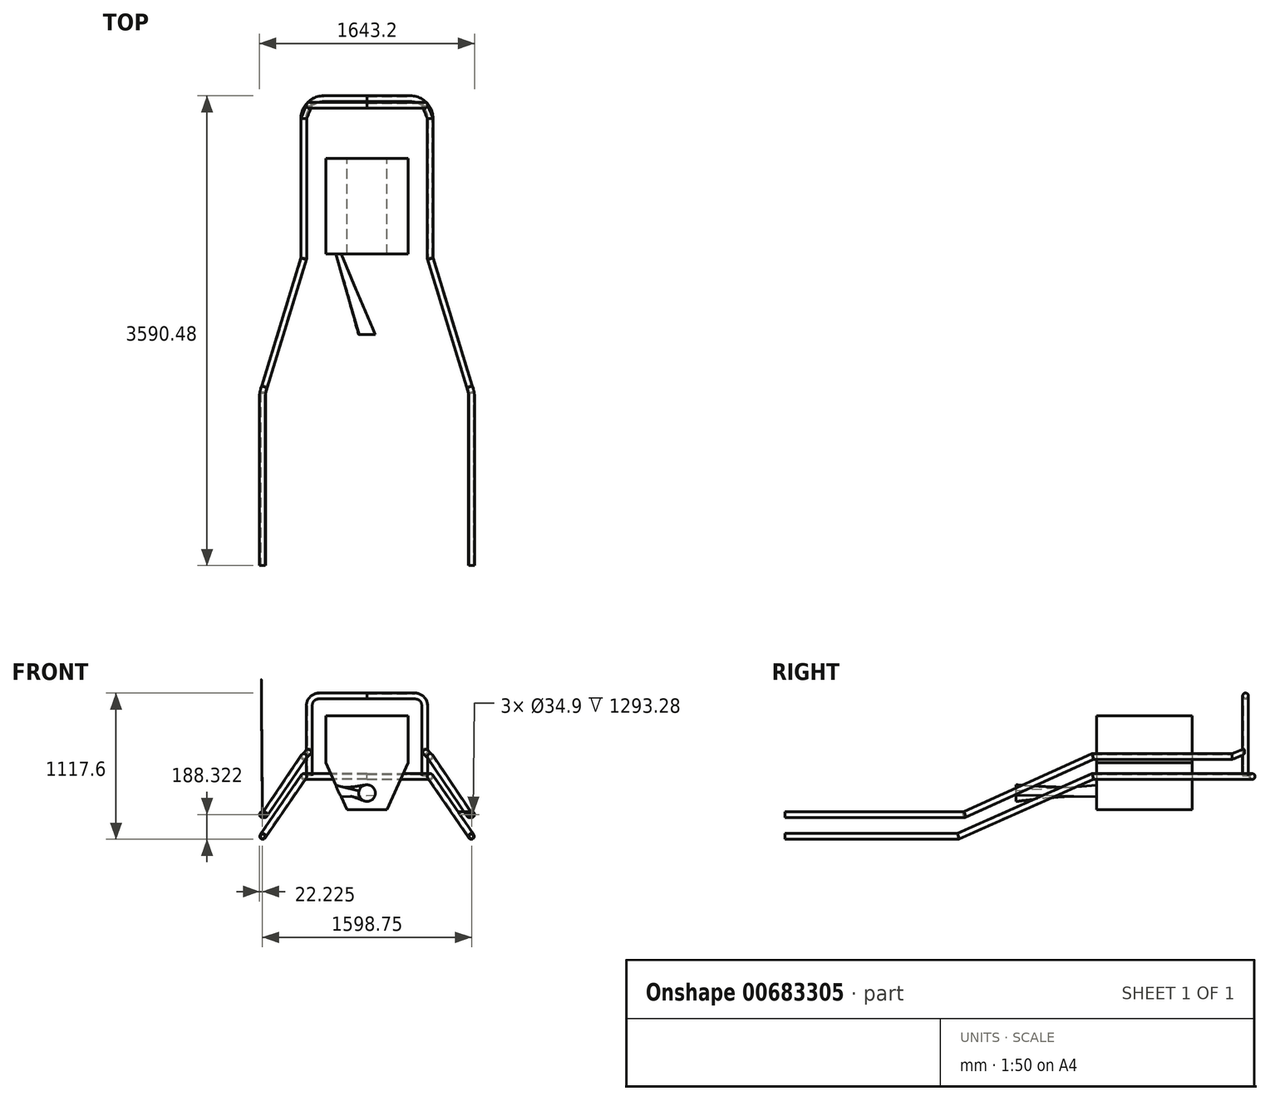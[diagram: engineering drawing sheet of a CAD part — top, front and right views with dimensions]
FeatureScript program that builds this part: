
annotation { "Feature Type Name" : "Feature", "Feature Type Description" : "" }
export const myFeature = defineFeature(function(context is Context, id is Id, definition is map)
    precondition{}
    {
        {
            var Q0;
            Q0=qCreatedBy(makeId("Front.planeOp"),FACE);
            var sketch = newSketch(context, id + "F0", { "sketchPlane" : qUnion([Q0])});
            skLineSegment(sketch, "E0", {"start": v(0, 0) * mm, "end": v(0, 717.55) * mm});
            skLineSegment(sketch, "E1", {"start": v(0, 717.55) * mm, "end": v(-314.33, 717.55) * mm});
            skLineSegment(sketch, "E2", {"start": v(-314.33, 717.55) * mm, "end": v(-314.33, 358.77) * mm});
            skLineSegment(sketch, "E3", {"start": v(0, 0) * mm, "end": v(-152.4, 0) * mm});
            skLineSegment(sketch, "E4", {"start": v(-314.33, 358.77) * mm, "end": v(-152.4, 0) * mm});
            skLineSegment(sketch, "E5.MirrorCS", {"start": v(0, 0) * mm, "end": v(152.4, 0) * mm});
            skLineSegment(sketch, "E6.MirrorCS", {"start": v(0, 717.55) * mm, "end": v(314.33, 717.55) * mm});
            skLineSegment(sketch, "E7.MirrorCS", {"start": v(314.33, 358.77) * mm, "end": v(152.4, 0) * mm});
            skLineSegment(sketch, "E8.MirrorCS", {"start": v(314.33, 717.55) * mm, "end": v(314.33, 358.77) * mm});
            skSolve(sketch);
        }
        {
            var Q0;
            Q0=makeQuery(id+"F0.imprint","IMPRINT",FACE,{"disambiguationData":[TD([[makeQuery(id+"F0.imprint","IMPRINT",EDGE,{"derivedFrom":sQuery(id+"F0.wireOp",EDGE,"E0")}),1.0]])]});
            var Q1;
            Q1=makeQuery(id+"F0.imprint","IMPRINT",FACE,{"disambiguationData":[TD([[makeQuery(id+"F0.imprint","IMPRINT",EDGE,{"derivedFrom":sQuery(id+"F0.wireOp",EDGE,"E0")}),-1.0]])]});
            extrude(context, id + "F1", {"entities" : qUnion([Q0, Q1]), "depth" : 730.25 * mm, "offsetDistance" : 25.4 * mm});
        }
        {
            var Q0;
            Q0=makeQuery(id+"F1.opExtrude","CAP_FACE",FACE,{"disambiguationData":[OSD([sQuery(id+"F0.wireOp",EDGE,"E1"),sQuery(id+"F0.wireOp",EDGE,"E2"),sQuery(id+"F0.wireOp",EDGE,"E3"),sQuery(id+"F0.wireOp",EDGE,"E4"),sQuery(id+"F0.wireOp",EDGE,"E5.MirrorCS"),sQuery(id+"F0.wireOp",EDGE,"E6.MirrorCS"),sQuery(id+"F0.wireOp",EDGE,"E7.MirrorCS"),sQuery(id+"F0.wireOp",EDGE,"E8.MirrorCS")])],"isStart":false});
            var sketch = newSketch(context, id + "F2", { "sketchPlane" : qUnion([Q0])});
            skCircle(sketch, "E9", {"center": v(0, 241.3) * mm, "radius": 242.89 * mm});
            skSolve(sketch);
        }
        {
            var Q0;
            Q0=makeQuery(id+"F2.imprint","IMPRINT",FACE,{"disambiguationData":[TD([[makeQuery(id+"F2.imprint","IMPRINT",EDGE,{"derivedFrom":makeQuery(id+"F1.opExtrude","CAP_EDGE",EDGE,{"disambiguationData":[OSD([sQuery(id+"F0.wireOp",EDGE,"E2")])],"isStart":false})}),1.0]])]});
            cPlane(context, id + "F3", {"entities" : qUnion([Q0]), "cplaneType" : CPlaneType.OFFSET, "offset" : 615.95 * mm, "width" : 152.4 * mm, "height" : 152.4 * mm});
        }
        {
            var Q0;
            Q0=qCreatedBy(id+"F3.planeOp",FACE);
            var sketch = newSketch(context, id + "F4", { "sketchPlane" : qUnion([Q0])});
            skCircle(sketch, "E10", {"center": v(0, 127) * mm, "radius": 63.5 * mm});
            skSolve(sketch);
        }
        {
            var Q1;
            {var subQ0=sQuery(id+"F2.wireOp",EDGE,"E9");var subQ1=makeQuery(id+"F1.opExtrude","CAP_EDGE",EDGE,{"disambiguationData":[OSD([sQuery(id+"F0.wireOp",EDGE,"E4")])],"isStart":false});var subQ2=makeQuery(id+"F2.imprint","INTERSECT",VERTEX,{"disambiguationData":[OD(1.0)],"derivedFrom":[subQ1,subQ0]});Q1=makeQuery(id+"F2.imprint","IMPRINT",FACE,{"disambiguationData":[TD([[makeQuery(id+"F2.imprint","IMPRINT",EDGE,{"disambiguationData":[TD([[subQ2,1.0]])],"derivedFrom":subQ0}),1.0]])]});}
            var Q2;
            Q2=makeQuery(id+"F4.imprint","IMPRINT",FACE,{"disambiguationData":[TD([[makeQuery(id+"F4.imprint","IMPRINT",EDGE,{"derivedFrom":sQuery(id+"F4.wireOp",EDGE,"E10")}),1.0]])]});
            loft(context, id + "F5", {"operationType" : NewBodyOperationType.ADD, "sheetProfilesArray" : [{ "sheetProfileEntities" : qUnion([Q1]) }, { "sheetProfileEntities" : qUnion([Q2]) }]});
        }
        {
            var Q0;
            Q0=makeQuery(id+"F1.opExtrude","SWEPT_FACE",FACE,{"disambiguationData":[OSD([sQuery(id+"F0.wireOp",EDGE,"E2")])]});
            cPlane(context, id + "F6", {"entities" : qUnion([Q0]), "cplaneType" : CPlaneType.OFFSET, "offset" : 317.5 * mm, "oppositeDirection" : true, "width" : 152.4 * mm, "height" : 152.4 * mm});
        }
        {
            var Q0;
            Q0=qCreatedBy(id+"F6.planeOp",FACE);
            var sketch = newSketch(context, id + "F7", { "sketchPlane" : qUnion([Q0])});
            skLineSegment(sketch, "E11.bottom", {"start": v(836.32, 471.65) * mm, "end": v(1187.86, 471.65) * mm});
            skLineSegment(sketch, "E11.top", {"start": v(836.32, 316.37) * mm, "end": v(1187.86, 316.37) * mm});
            skLineSegment(sketch, "E11.left", {"start": v(836.32, 471.65) * mm, "end": v(836.32, 316.37) * mm});
            skLineSegment(sketch, "E11.right", {"start": v(1187.86, 471.65) * mm, "end": v(1187.86, 316.37) * mm});
            skSolve(sketch);
        }
        {
            var Q0;
            Q0=makeQuery(id+"F7.imprint","IMPRINT",FACE,{"disambiguationData":[TD([[makeQuery(id+"F7.imprint","IMPRINT",EDGE,{"derivedFrom":sQuery(id+"F7.wireOp",EDGE,"E11.bottom")}),-1.0]])]});
            extrude(context, id + "F8", {"entities" : qUnion([Q0]), "operationType" : NewBodyOperationType.REMOVE, "endBound" : BoundingType.THROUGH_ALL, "oppositeDirection" : true, "depth" : 508 * mm, "offsetDistance" : 25.4 * mm, "hasSecondDirection" : true, "secondDirectionBound" : SecondDirectionBoundingType.THROUGH_ALL, "secondDirectionOppositeDirection" : false, "secondDirectionDepth" : 25.4 * mm});
        }
        {
            var Q0;
            Q0=makeQuery(id+"F1.opExtrude","SWEPT_FACE",FACE,{"disambiguationData":[OSD([sQuery(id+"F0.wireOp",EDGE,"E3"),sQuery(id+"F0.wireOp",EDGE,"E5.MirrorCS")])]});
            cPlane(context, id + "F9", {"entities" : qUnion([Q0]), "cplaneType" : CPlaneType.OFFSET, "offset" : 0 * mm, "width" : 152.4 * mm, "height" : 152.4 * mm});
        }
        {
            var Q0;
            Q0=qCreatedBy(id+"F9.planeOp",FACE);
            var sketch = newSketch(context, id + "F10", { "sketchPlane" : qUnion([Q0])});
            skLineSegment(sketch, "E12", {"start": v(0, 0) * mm, "end": v(0, -228.6) * mm});
            skLineSegment(sketch, "E13", {"start": v(0, -228.6) * mm, "end": v(-390.53, -228.6) * mm});
            skLineSegment(sketch, "E14", {"start": v(-517.52, -101.6) * mm, "end": v(-517.52, 730.25) * mm});
            skLineSegment(sketch, "E15", {"start": v(-669.92, 882.65) * mm, "end": v(-736.6, 882.65) * mm});
            skLineSegment(sketch, "E16", {"start": v(-889, 1035.05) * mm, "end": v(-889, 2711.45) * mm});
            skPoint(sketch, "E17.visualSharp", {"position": v(-517.52, -228.6) * mm});
            skArc(sketch, "E17.filletArc", {"start": v(-517.52, -101.6) * mm, "mid": v(-480.33, -191.4) * mm, "end": v(-390.53, -228.6) * mm});
            skPoint(sketch, "E18.visualSharp", {"position": v(-517.52, 882.65) * mm});
            skArc(sketch, "E18.filletArc", {"start": v(-517.52, 730.25) * mm, "mid": v(-562.16, 838.01) * mm, "end": v(-669.92, 882.65) * mm});
            skPoint(sketch, "E19.visualSharp", {"position": v(-889, 882.65) * mm});
            skArc(sketch, "E19.filletArc", {"start": v(-889, 1035.05) * mm, "mid": v(-844.36, 927.29) * mm, "end": v(-736.6, 882.65) * mm});
            skLineSegment(sketch, "E20.MirrorCS", {"start": v(669.92, 882.65) * mm, "end": v(736.6, 882.65) * mm});
            skArc(sketch, "E21.MirrorCS", {"start": v(517.52, -101.6) * mm, "mid": v(480.33, -191.4) * mm, "end": v(390.53, -228.6) * mm});
            skArc(sketch, "E22.MirrorCS", {"start": v(517.52, 730.25) * mm, "mid": v(562.16, 838.01) * mm, "end": v(669.92, 882.65) * mm});
            skArc(sketch, "E23.MirrorCS", {"start": v(889, 1035.05) * mm, "mid": v(844.36, 927.29) * mm, "end": v(736.6, 882.65) * mm});
            skLineSegment(sketch, "E24.MirrorCS", {"start": v(517.52, -101.6) * mm, "end": v(517.52, 730.25) * mm});
            skLineSegment(sketch, "E25.MirrorCS", {"start": v(0, -228.6) * mm, "end": v(390.53, -228.6) * mm});
            skLineSegment(sketch, "E26.MirrorCS", {"start": v(889, 1035.05) * mm, "end": v(889, 2711.45) * mm});
            skPoint(sketch, "E27.MirrorP", {"position": v(517.52, -228.6) * mm});
            skPoint(sketch, "E28.MirrorP", {"position": v(517.52, 882.65) * mm});
            skPoint(sketch, "E29.MirrorP", {"position": v(889, 882.65) * mm});
            skSolve(sketch);
        }
        {
            var Q0;
            Q0=qCreatedBy(id+"F3.planeOp",FACE);
            cPlane(context, id + "F11", {"entities" : qUnion([Q0]), "cplaneType" : CPlaneType.OFFSET, "offset" : 1365.25 * mm, "width" : 152.4 * mm, "height" : 152.4 * mm});
        }
        {
            var Q0;
            Q0=makeQuery(id+"F1.opExtrude","SWEPT_FACE",FACE,{"disambiguationData":[OSD([sQuery(id+"F0.wireOp",EDGE,"E2")])]});
            cPlane(context, id + "F12", {"entities" : qUnion([Q0]), "cplaneType" : CPlaneType.OFFSET, "offset" : 168.27 * mm, "width" : 152.4 * mm, "height" : 152.4 * mm});
        }
        {
            var Q0;
            Q0=qCreatedBy(id+"F12.planeOp",FACE);
            var sketch = newSketch(context, id + "F13", { "sketchPlane" : qUnion([Q0])});
            skLineSegment(sketch, "E30", {"start": v(-127, 0) * mm, "end": v(-127, 641.35) * mm});
            skLineSegment(sketch, "E31", {"start": v(25.4, 793.75) * mm, "end": v(728.15, 793.75) * mm});
            skPoint(sketch, "E32.visualSharp", {"position": v(-127, 793.75) * mm});
            skArc(sketch, "E32.filletArc", {"start": v(25.4, 793.75) * mm, "mid": v(-82.36, 749.11) * mm, "end": v(-127, 641.35) * mm});
            skSolve(sketch);
        }
        {
            var Q0;
            Q0=qCreatedBy(id+"F9.planeOp",FACE);
            cPlane(context, id + "F14", {"entities" : qUnion([Q0]), "cplaneType" : CPlaneType.OFFSET, "offset" : 254 * mm, "oppositeDirection" : true, "width" : 152.4 * mm, "height" : 152.4 * mm});
        }
        {
            var Q0;
            Q0=qCreatedBy(id+"F14.planeOp",FACE);
            var sketch = newSketch(context, id + "F15", { "sketchPlane" : qUnion([Q0])});
            skLineSegment(sketch, "E33", {"start": v(-482.6, 762) * mm, "end": v(-482.6, -304.8) * mm});
            skPoint(sketch, "E34.visualSharp", {"position": v(482.6, -457.2) * mm});
            skPoint(sketch, "E35.visualSharp", {"position": v(-482.6, -457.2) * mm});
            skArc(sketch, "E35.filletArc", {"start": v(-482.6, -304.8) * mm, "mid": v(-437.96, -412.56) * mm, "end": v(-330.2, -457.2) * mm});
            skLineSegment(sketch, "E36", {"start": v(-330.2, -457.2) * mm, "end": v(0, -457.2) * mm});
            skSolve(sketch);
        }
        {
            var Q0;
            Q0=makeQuery(id+"F1.opExtrude","CAP_EDGE",EDGE,{"disambiguationData":[OSD([sQuery(id+"F0.wireOp",EDGE,"E2")])],"isStart":false});
            cPlane(context, id + "F16", {"entities" : qUnion([Q0]), "cplaneType" : CPlaneType.LINE_ANGLE, "offset" : 25.4 * mm, "angle" : 17 * degree, "width" : 152.4 * mm, "height" : 152.4 * mm});
        }
        {
            var Q0;
            Q0=qCreatedBy(id+"F16.planeOp",FACE);
            cPlane(context, id + "F17", {"entities" : qUnion([Q0]), "cplaneType" : CPlaneType.OFFSET, "offset" : 151.64 * mm, "width" : 152.4 * mm, "height" : 152.4 * mm});
        }
        {
            var Q0;
            Q0=qCreatedBy(id+"F17.planeOp",FACE);
            var sketch = newSketch(context, id + "F18", { "sketchPlane" : qUnion([Q0])});
            skLineSegment(sketch, "E37", {"start": v(869.8, 254) * mm, "end": v(1945.04, -203.2) * mm});
            skSolve(sketch);
        }
        {
            var Q0;
            Q0=qCreatedBy(id+"F14.planeOp",FACE);
            cPlane(context, id + "F19", {"entities" : qUnion([Q0]), "cplaneType" : CPlaneType.OFFSET, "offset" : 457.2 * mm, "width" : 152.4 * mm, "height" : 152.4 * mm});
        }
        {
            var Q0;
            Q0=qCreatedBy(id+"F19.planeOp",FACE);
            var sketch = newSketch(context, id + "F20", { "sketchPlane" : qUnion([Q0])});
            skLineSegment(sketch, "E38", {"start": v(-796.97, 1790.25) * mm, "end": v(-796.97, 3111.05) * mm});
            skSolve(sketch);
        }
        {
            var Q0;
            Q0=qCreatedBy(makeId("Right.planeOp"),FACE);
            var sketch = newSketch(context, id + "F21", { "sketchPlane" : qUnion([Q0])});
            skCircle(sketch, "E39", {"center": v(457.2, 254) * mm, "radius": 22.23 * mm});
            skCircle(sketch, "E40", {"center": v(457.2, 254) * mm, "radius": 17.45 * mm});
            skSolve(sketch);
        }
        {
            var Q0;
            Q0=qCreatedBy(id+"F14.planeOp",FACE);
            cPlane(context, id + "F22", {"entities" : qUnion([Q0]), "cplaneType" : CPlaneType.OFFSET, "offset" : 152.4 * mm, "oppositeDirection" : true, "width" : 152.4 * mm, "height" : 152.4 * mm});
        }
        {
            var Q0;
            Q0=qCreatedBy(id+"F22.planeOp",FACE);
            var sketch = newSketch(context, id + "F23", { "sketchPlane" : qUnion([Q0])});
            skLineSegment(sketch, "E41", {"start": v(-482.6, -304.8) * mm, "end": v(-482.6, 762) * mm});
            skSolve(sketch);
        }
        {
            var Q0;
            Q0=qCreatedBy(id+"F17.planeOp",FACE);
            var sketch = newSketch(context, id + "F24", { "sketchPlane" : qUnion([Q0])});
            skLineSegment(sketch, "E42", {"start": v(869.8, 406.4) * mm, "end": v(1895.64, -37.1) * mm});
            skSolve(sketch);
        }
        {
            var Q0;
            Q0=qCreatedBy(id+"F19.planeOp",FACE);
            cPlane(context, id + "F25", {"entities" : qUnion([Q0]), "cplaneType" : CPlaneType.OFFSET, "offset" : 166.1 * mm, "oppositeDirection" : true, "width" : 152.4 * mm, "height" : 152.4 * mm});
        }
        {
            var Q0;
            Q0=qCreatedBy(id+"F25.planeOp",FACE);
            var sketch = newSketch(context, id + "F26", { "sketchPlane" : qUnion([Q0])});
            skLineSegment(sketch, "E43", {"start": v(-799.38, 1816.95) * mm, "end": v(-799.38, 3110.23) * mm});
            skLineSegment(sketch, "E44", {"start": v(-782.52, 1743.01) * mm, "end": v(-790.74, 1766.4) * mm});
            skPoint(sketch, "E45.visualSharp", {"position": v(-799.38, 1790.94) * mm});
            skArc(sketch, "E45.filletArc", {"start": v(-799.38, 1816.95) * mm, "mid": v(-797.2, 1791.3) * mm, "end": v(-790.74, 1766.4) * mm});
            skSolve(sketch);
        }
        {
            var Q0;
            Q0=makeQuery(id+"F21.imprint","IMPRINT",FACE,{"disambiguationData":[TD([[makeQuery(id+"F21.imprint","IMPRINT",EDGE,{"derivedFrom":sQuery(id+"F21.wireOp",EDGE,"E39")}),1.0]])]});
            var Q1;
            Q1=sQuery(id+"F15.wireOp",EDGE,"E36");
            var Q2;
            Q2=sQuery(id+"F15.wireOp",EDGE,"E35.filletArc");
            var Q3;
            Q3=sQuery(id+"F15.wireOp",EDGE,"E33");
            var Q4;
            Q4=sQuery(id+"F18.wireOp",EDGE,"E37");
            var Q5;
            Q5=sQuery(id+"F20.wireOp",EDGE,"E38");
            sweep(context, id + "F27", {"profiles" : qUnion([Q0]), "path" : qUnion([Q1, Q2, Q3, Q4, Q5])});
        }
        {
            var Q0;
            Q0=makeQuery(id+"F27.opSweep","SWEPT_BODY",BODY,{"disambiguationData":[OSD([sQuery(id+"F20.wireOp",EDGE,"E38"),sQuery(id+"F21.wireOp",EDGE,"E39"),sQuery(id+"F21.wireOp",EDGE,"E40")])]});
            var Q1;
            Q1=qCreatedBy(makeId("Right.planeOp"),FACE);
            mirror(context, id + "F28", {"operationType" : NewBodyOperationType.ADD, "entities" : qUnion([Q0]), "mirrorPlane" : qUnion([Q1])});
        }
        {
            var Q0;
            Q0=makeQuery(id+"F27.opSweep","CAP_FACE",FACE,{"disambiguationData":[OSD([sQuery(id+"F20.wireOp",VERTEX,"E38.end"),sQuery(id+"F21.wireOp",EDGE,"E39"),sQuery(id+"F21.wireOp",EDGE,"E40")])],"isStart":false});
            var sketch = newSketch(context, id + "F29", { "sketchPlane" : qUnion([Q0])});
            skCircle(sketch, "E46", {"center": v(-799.38, -37.1) * mm, "radius": 22.23 * mm});
            skCircle(sketch, "E47", {"center": v(-799.38, -37.1) * mm, "radius": 17.45 * mm});
            skSolve(sketch);
        }
        {
            var Q0;
            Q0=makeQuery(id+"F29.imprint","IMPRINT",FACE,{"disambiguationData":[TD([[makeQuery(id+"F29.imprint","IMPRINT",EDGE,{"derivedFrom":sQuery(id+"F29.wireOp",EDGE,"E46")}),1.0]])]});
            var Q1;
            Q1=sQuery(id+"F26.wireOp",EDGE,"E43");
            var Q2;
            Q2=sQuery(id+"F26.wireOp",EDGE,"E44");
            var Q3;
            Q3=sQuery(id+"F26.wireOp",EDGE,"E45.filletArc");
            var Q4;
            Q4=sQuery(id+"F24.wireOp",EDGE,"E42");
            var Q5;
            Q5=sQuery(id+"F23.wireOp",EDGE,"E41");
            sweep(context, id + "F30", {"profiles" : qUnion([Q0]), "path" : qUnion([Q1, Q2, Q3, Q4, Q5])});
        }
        {
            var Q0;
            Q0=makeQuery(id+"F30.opSweep","SWEPT_BODY",BODY,{"disambiguationData":[OSD([sQuery(id+"F23.wireOp",EDGE,"E41"),sQuery(id+"F29.wireOp",EDGE,"E46"),sQuery(id+"F29.wireOp",EDGE,"E47")])]});
            var Q1;
            Q1=qCreatedBy(makeId("Right.planeOp"),FACE);
            mirror(context, id + "F31", {"entities" : qUnion([Q0]), "mirrorPlane" : qUnion([Q1])});
        }
        {
            var Q0;
            Q0=makeQuery(id+"F1.opExtrude","CAP_FACE",FACE,{"disambiguationData":[OSD([sQuery(id+"F0.wireOp",EDGE,"E1"),sQuery(id+"F0.wireOp",EDGE,"E2"),sQuery(id+"F0.wireOp",EDGE,"E3"),sQuery(id+"F0.wireOp",EDGE,"E4"),sQuery(id+"F0.wireOp",EDGE,"E5.MirrorCS"),sQuery(id+"F0.wireOp",EDGE,"E6.MirrorCS"),sQuery(id+"F0.wireOp",EDGE,"E7.MirrorCS"),sQuery(id+"F0.wireOp",EDGE,"E8.MirrorCS")])],"isStart":true});
            cPlane(context, id + "F32", {"entities" : qUnion([Q0]), "cplaneType" : CPlaneType.OFFSET, "offset" : 406.4 * mm, "width" : 152.4 * mm, "height" : 152.4 * mm});
        }
        {
            var Q0;
            Q0=qCreatedBy(id+"F32.planeOp",FACE);
            var sketch = newSketch(context, id + "F33", { "sketchPlane" : qUnion([Q0])});
            skLineSegment(sketch, "E48", {"start": v(441.32, 261.2) * mm, "end": v(441.32, 793.75) * mm});
            skLineSegment(sketch, "E49", {"start": v(365.13, 869.95) * mm, "end": v(0, 869.95) * mm});
            skPoint(sketch, "E50.visualSharp", {"position": v(441.33, 869.95) * mm});
            skArc(sketch, "E50.filletArc", {"start": v(441.33, 793.75) * mm, "mid": v(419, 847.63) * mm, "end": v(365.13, 869.95) * mm});
            skSolve(sketch);
        }
        {
            var Q0;
            Q0=qCreatedBy(makeId("Right.planeOp"),FACE);
            var sketch = newSketch(context, id + "F34", { "sketchPlane" : qUnion([Q0])});
            skCircle(sketch, "E51", {"center": v(406.4, 869.95) * mm, "radius": 22.23 * mm});
            skCircle(sketch, "E52", {"center": v(406.4, 869.95) * mm, "radius": 17.45 * mm});
            skSolve(sketch);
        }
        {
            var Q0;
            Q0=makeQuery(id+"F34.imprint","IMPRINT",FACE,{"disambiguationData":[TD([[makeQuery(id+"F34.imprint","IMPRINT",EDGE,{"derivedFrom":sQuery(id+"F34.wireOp",EDGE,"E51")}),1.0]])]});
            var Q1;
            Q1=sQuery(id+"F33.wireOp",EDGE,"E49");
            var Q2;
            Q2=sQuery(id+"F33.wireOp",EDGE,"E50.filletArc");
            var Q3;
            Q3=sQuery(id+"F33.wireOp",EDGE,"E48");
            sweep(context, id + "F35", {"profiles" : qUnion([Q0]), "path" : qUnion([Q1, Q2, Q3])});
        }
        {
            var Q0;
            Q0=makeQuery(id+"F35.opSweep","SWEPT_BODY",BODY,{"disambiguationData":[OSD([sQuery(id+"F33.wireOp",EDGE,"E48"),sQuery(id+"F34.wireOp",EDGE,"E51"),sQuery(id+"F34.wireOp",EDGE,"E52")])]});
            var Q1;
            Q1=qCreatedBy(makeId("Right.planeOp"),FACE);
            mirror(context, id + "F36", {"entities" : qUnion([Q0]), "mirrorPlane" : qUnion([Q1])});
        }
        {
            var Q0;
            Q0=makeQuery(id+"F1.opExtrude","CAP_EDGE",EDGE,{"disambiguationData":[OSD([sQuery(id+"F0.wireOp",EDGE,"E2")])],"isStart":true});
            cPlane(context, id + "F37", {"entities" : qUnion([Q0]), "cplaneType" : CPlaneType.LINE_ANGLE, "offset" : 25.4 * mm, "angle" : 22 * degree, "width" : 152.4 * mm, "height" : 152.4 * mm});
        }
        {
            var Q0;
            Q0=qCreatedBy(id+"F37.planeOp",FACE);
            cPlane(context, id + "F38", {"entities" : qUnion([Q0]), "cplaneType" : CPlaneType.OFFSET, "offset" : 266.7 * mm, "width" : 152.4 * mm, "height" : 152.4 * mm});
        }
        {
            var Q0;
            Q0=qCreatedBy(id+"F38.planeOp",FACE);
            var sketch = newSketch(context, id + "F39", { "sketchPlane" : qUnion([Q0])});
            skLineSegment(sketch, "E53", {"start": v(-107.55, 408.52) * mm, "end": v(-212.86, 448.13) * mm});
            skSolve(sketch);
        }
        {
            var Q0;
            Q0=makeQuery(id+"F30.opSweep","CAP_FACE",FACE,{"disambiguationData":[OSD([sQuery(id+"F23.wireOp",VERTEX,"E41.start"),sQuery(id+"F29.wireOp",EDGE,"E46"),sQuery(id+"F29.wireOp",EDGE,"E47")])],"isStart":false});
            var sketch = newSketch(context, id + "F40", { "sketchPlane" : qUnion([Q0])});
            skCircle(sketch, "E54", {"center": v(482.6, 406.4) * mm, "radius": 17.45 * mm});
            skCircle(sketch, "E55", {"center": v(482.6, 406.4) * mm, "radius": 22.23 * mm});
            skSolve(sketch);
        }
        {
            var Q0;
            Q0=makeQuery(id+"F40.imprint","IMPRINT",FACE,{"disambiguationData":[TD([[makeQuery(id+"F40.imprint","IMPRINT",EDGE,{"derivedFrom":sQuery(id+"F40.wireOp",EDGE,"E54")}),1.0]])]});
            var Q1;
            Q1=sQuery(id+"F39.wireOp",EDGE,"E53");
            sweep(context, id + "F41", {"operationType" : NewBodyOperationType.ADD, "profiles" : qUnion([Q0]), "path" : qUnion([Q1]), "keepProfileOrientation" : true});
        }
        {
            var Q0;
            Q0=makeQuery(id+"F30.opSweep","SWEPT_BODY",BODY,{"disambiguationData":[OSD([sQuery(id+"F23.wireOp",EDGE,"E41"),sQuery(id+"F29.wireOp",EDGE,"E46"),sQuery(id+"F29.wireOp",EDGE,"E47")])]});
            var Q1;
            Q1=qCreatedBy(makeId("Right.planeOp"),FACE);
            mirror(context, id + "F42", {"entities" : qUnion([Q0]), "mirrorPlane" : qUnion([Q1])});
        }
        {
            var Q0;
            Q0=makeQuery(id+"F1.opExtrude","CAP_EDGE",EDGE,{"disambiguationData":[OSD([sQuery(id+"F0.wireOp",EDGE,"E1"),sQuery(id+"F0.wireOp",EDGE,"E6.MirrorCS")])],"isStart":true});
            cPlane(context, id + "F43", {"entities" : qUnion([Q0]), "cplaneType" : CPlaneType.LINE_ANGLE, "offset" : 25.4 * mm, "angle" : 5 * degree, "oppositeDirection" : true, "width" : 152.4 * mm, "height" : 152.4 * mm});
        }
        {
            var Q0;
            Q0=qCreatedBy(id+"F43.planeOp",FACE);
            cPlane(context, id + "F44", {"entities" : qUnion([Q0]), "cplaneType" : CPlaneType.OFFSET, "offset" : 415.92 * mm, "oppositeDirection" : true, "width" : 152.4 * mm, "height" : 152.4 * mm});
        }
    });
